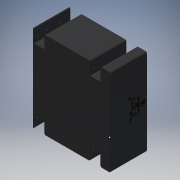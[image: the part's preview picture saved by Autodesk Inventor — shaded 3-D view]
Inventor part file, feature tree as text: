
AUTODESK INVENTOR PART (.ipt)
format: ipt  version: 2016 (Build 200138000, 138)  size: 590,336 bytes
history: native  units: mm
features: extrude x27, sketch x27, fillet x1
ambient origin geometry x8: Origin, YZ Plane, XZ Plane, XY Plane, X Axis, Y Axis, Z Axis, Center Point
bodies: Solid1 (feature_tree)
feature tree (55):
  extrude  "Extrusion1"  Depth=20.0mm
  extrude  "Extrusion2"  Depth=170.0mm
  extrude  "Extrusion3"  Depth=25.0mm
  extrude  "Extrusion4"  Depth=25.0mm
  extrude  "Extrusion5"  Depth=20.0mm
  extrude  "Extrusion6"  Depth=20.0mm
  extrude  "Extrusion7"  Depth=90.0mm
  extrude  "Extrusion8"  Depth=2.0mm TaperAngle=0.0deg
  extrude  "Extrusion9"  Depth=2.0mm
  extrude  "Extrusion10"  Depth=2.0mm
  extrude  "Extrusion11"  Depth=2.0mm
  extrude  "Extrusion12"  Depth=2.0mm
  extrude  "Extrusion13"  Depth=2.0mm
  extrude  "Extrusion14"  Depth=2.0mm
  extrude  "Extrusion15"  Depth=2.0mm
  extrude  "Extrusion16"  Depth=69.0mm TaperAngle=0.0deg
  extrude  "Extrusion17"  Depth=10.0mm TaperAngle=0.0deg
  extrude  "Extrusion18"  Depth=10.0mm
  extrude  "Extrusion32"  Depth=4.0mm TaperAngle=0.0deg
  extrude  "Extrusion33"  Depth=10.0mm
  extrude  "Extrusion34"  Depth=4.0mm TaperAngle=0.0deg
  extrude  "Extrusion35"  Depth=10.0mm
  extrude  "Extrusion53"  Depth=4.0mm TaperAngle=0.0deg
  fillet  "Fillet1"  Radius=7.0mm
  extrude  "Extrusion54"  Depth=10.0mm
  extrude  "Extrusion55"  Depth=4.0mm
  extrude  "Extrusion56"  Depth=4.0mm
  extrude  "Extrusion57"  Depth=7.0mm
  sketch  "Sketch1"  dims[d0=2.0mm d1=20.0mm]
  sketch  "Sketch2"  dims[d2=20.0mm d3=170.0mm]
  sketch  "Sketch4"  dims[d4=170.0mm d6=25.0mm]
  sketch  "Sketch5"  dims[d9=25.0mm d10=25.0mm]
  sketch  "Sketch6"  dims[d11=25.0mm d12=20.0mm]
  sketch  "Sketch7"  dims[d13=90.0mm d14=20.0mm]
  sketch  "Sketch8"  dims[d15=2.0mm d16=90.0mm]
  sketch  "Sketch9"  dims[d17=20.0mm d18=2.0mm d19=0.0mm]
  sketch  "Sketch10"  dims[d20=4.0mm d21=2.0mm]
  sketch  "Sketch11"  dims[d22=2.0mm d23=2.0mm]
  sketch  "Sketch12"  dims[d26=4.0mm d27=2.0mm]
  sketch  "Sketch13"  dims[d28=2.0mm d29=2.0mm]
  sketch  "Sketch14"  dims[d30=2.0mm d31=2.0mm]
  sketch  "Sketch15"  dims[d32=4.0mm d33=2.0mm]
  sketch  "Sketch16"  dims[d34=2.0mm d35=2.0mm]
  sketch  "Sketch17"  dims[d36=4.0mm d37=69.0mm d38=0.0mm]
  sketch  "Sketch18"  dims[d39=2.0mm d40=10.0mm d41=0.0mm]
  sketch  "Sketch19"  dims[d42=7.0mm d43=10.0mm]
  sketch  "Sketch33"  dims[d44=3.2mm d45=4.0mm d46=0.0mm]
  sketch  "Sketch34"  dims[d47=7.0mm d48=10.0mm]
  sketch  "Sketch35"  dims[d49=3.2mm d50=4.0mm d51=0.0mm]
  sketch  "Sketch36"  dims[d52=7.0mm d53=10.0mm]
  sketch  "Sketch55"  dims[d54=3.2mm d55=4.0mm d56=0.0mm d57=7.0mm]
  sketch  "Sketch56"  dims[d58=10.0mm d59=3.2mm]
  sketch  "Sketch57"  dims[d60=4.0mm d61=0.0mm d64=3.2mm]
  sketch  "Sketch58"  dims[d65=4.0mm d66=0.0mm d69=3.2mm]
  sketch  "Sketch59"  dims[d70=4.0mm d71=0.0mm d72=7.0mm d73=10.0mm d74=3.2mm d75=4.0mm d76=0.0mm d77=7.0mm d79=3.2mm d80=4.0mm d81=0.0mm d82=5.0mm d83=3.0mm d84=15.0mm d85=3.0mm d86=20.0mm d87=25.0mm d88=3.0mm d89=3.0mm d90=2.0mm d91=0.0mm d92=7.0mm d93=2.625mm d94=3.0mm d95=4.0mm d96=0.0mm d97=7.0mm d98=2.625mm d99=3.0mm d100=4.0mm d101=0.0mm d102=7.0mm d103=2.625mm d104=3.0mm d105=4.0mm d106=0.0mm d107=7.0mm d108=2.625mm d109=3.0mm d110=4.0mm d111=0.0mm d112=25.0mm d113=25.0mm d114=25.0mm d115=25.0mm d116=29.0mm d117=14.5mm d118=15.0mm d119=7.0mm d120=6.0mm d121=6.0mm d122=6.0mm d123=3.0mm d124=6.0mm d125=6.0mm d126=6.0mm d127=6.0mm d128=67.0mm d129=0.0mm d130=3.0mm d131=3.0mm d132=3.0mm d133=67.0mm d134=0.0mm d135=6.0mm d136=3.0mm d137=3.0mm d138=3.0mm d139=3.0mm d202=3.0mm d203=3.0mm d299=11.0mm d300=2.5mm d301=5.0mm d302=5.0mm d303=4.0mm d304=0.0mm d305=11.0mm d306=2.5mm d307=5.0mm d308=5.0mm d309=4.0mm d310=0.0mm d311=11.0mm d312=2.5mm d313=5.0mm d314=5.0mm d315=4.0mm d316=0.0mm d317=11.0mm d318=2.5mm d319=5.0mm d320=5.0mm d321=4.0mm d322=0.0mm d363=10.0mm d364=10.0mm d365=10.0mm d387=7.0mm d388=10.0mm d412=3.0mm d415=158.0mm d416=78.0mm d417=158.0mm d418=78.0mm d419=4.0mm d421=4.0mm d422=4.0mm d423=4.0mm d424=8.0mm d425=8.0mm d426=8.0mm d427=8.0mm d428=8.0mm d429=8.0mm d430=8.0mm d431=8.0mm d432=24.0mm d433=0.0mm d434=3.0mm d435=5.0mm d436=10.0mm d437=5.0mm d439=10.0mm d441=2.0mm d442=0.0mm d443=10.0mm d444=19.0mm d445=2.0mm d446=0.0mm d447=10.0mm d449=10.0mm d450=2.0mm d451=0.0mm d452=16.5mm d453=16.5mm d454=26.5mm d455=30.0mm d456=30.0mm d457=10.0mm d458=0.0mm]
